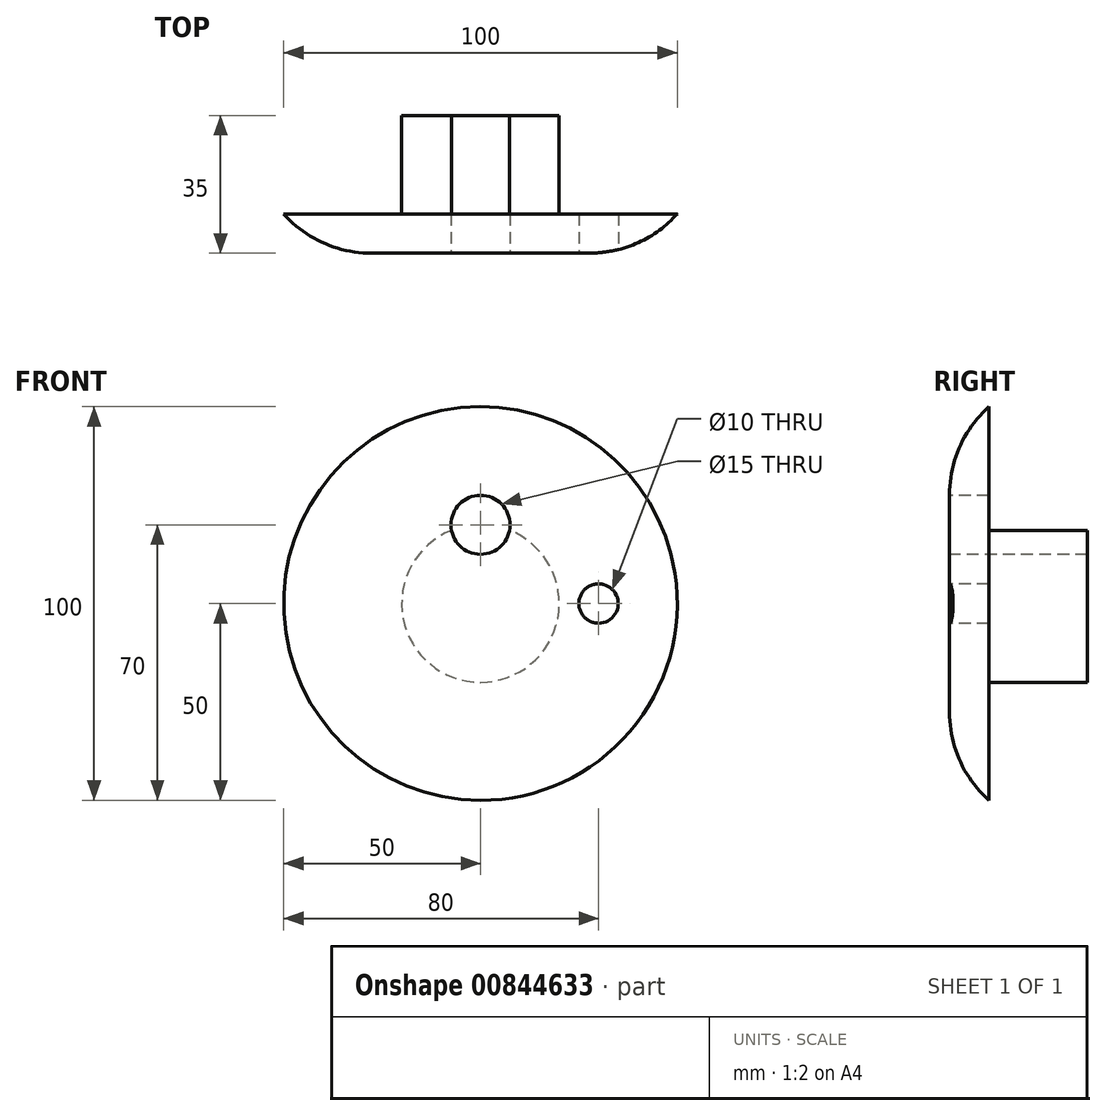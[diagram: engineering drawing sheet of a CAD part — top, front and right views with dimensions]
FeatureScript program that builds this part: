
annotation { "Feature Type Name" : "Feature", "Feature Type Description" : "" }
export const myFeature = defineFeature(function(context is Context, id is Id, definition is map)
    precondition{}
    {
        {
            var Q0;
            Q0=qCreatedBy(makeId("Front.planeOp"),FACE);
            var sketch = newSketch(context, id + "F0", { "sketchPlane" : qUnion([Q0])});
            skCircle(sketch, "E0", {"center": v(0, 0) * mm, "radius": 50 * mm});
            skSolve(sketch);
        }
        {
            var Q0;
            Q0=makeQuery(id+"F0.imprint","IMPRINT",FACE,{"disambiguationData":[TD([[makeQuery(id+"F0.imprint","IMPRINT",EDGE,{"derivedFrom":sQuery(id+"F0.wireOp",EDGE,"E0")}),1.0]])]});
            extrude(context, id + "F1", {"entities" : qUnion([Q0]), "depth" : 10 * mm, "offsetDistance" : 25 * mm});
        }
        {
            var Q0;
            Q0=makeQuery(id+"F1.opExtrude","CAP_FACE",FACE,{"disambiguationData":[OSD([sQuery(id+"F0.wireOp",EDGE,"E0")])],"isStart":true});
            var sketch = newSketch(context, id + "F2", { "sketchPlane" : qUnion([Q0])});
            skCircle(sketch, "E1", {"center": v(0, 0) * mm, "radius": 20 * mm});
            skSolve(sketch);
        }
        {
            var Q0;
            Q0 = qSketchRegion(id + "F2", true);
            extrude(context, id + "F3", {"entities" : qUnion([Q0]), "operationType" : NewBodyOperationType.ADD, "depth" : 25 * mm, "offsetDistance" : 25 * mm});
        }
        {
            var Q0;
            Q0=qCreatedBy(makeId("Front.planeOp"),FACE);
            cPlane(context, id + "F4", {"entities" : qUnion([Q0]), "cplaneType" : CPlaneType.OFFSET, "offset" : 10 * mm, "width" : 150 * mm, "height" : 150 * mm});
        }
        {
            var Q0;
            Q0=qCreatedBy(id+"F4.planeOp",FACE);
            var sketch = newSketch(context, id + "F5", { "sketchPlane" : qUnion([Q0])});
            skCircle(sketch, "E2", {"center": v(30, 0) * mm, "radius": 5 * mm});
            skSolve(sketch);
        }
        {
            var Q0;
            Q0 = qSketchRegion(id + "F5", true);
            extrude(context, id + "F6", {"entities" : qUnion([Q0]), "operationType" : NewBodyOperationType.REMOVE, "oppositeDirection" : true, "depth" : 85.64 * mm, "offsetDistance" : 25 * mm});
        }
        {
            var Q0;
            Q0=makeQuery(id+"F1.opExtrude","CAP_FACE",FACE,{"disambiguationData":[OSD([sQuery(id+"F0.wireOp",EDGE,"E0")])],"isStart":false});
            var sketch = newSketch(context, id + "F7", { "sketchPlane" : qUnion([Q0])});
            skCircle(sketch, "E3", {"center": v(0, 20) * mm, "radius": 7.5 * mm});
            skSolve(sketch);
        }
        {
            var Q0;
            Q0=makeQuery(id+"F7.imprint","IMPRINT",FACE,{"disambiguationData":[TD([[makeQuery(id+"F7.imprint","IMPRINT",EDGE,{"derivedFrom":sQuery(id+"F7.wireOp",EDGE,"E3")}),1.0]])]});
            extrude(context, id + "F8", {"entities" : qUnion([Q0]), "operationType" : NewBodyOperationType.REMOVE, "oppositeDirection" : true, "depth" : 57.22 * mm, "offsetDistance" : 25 * mm});
        }
        {
            var Q0;
            Q0=makeQuery(id+"F1.opExtrude","CAP_EDGE",EDGE,{"disambiguationData":[OSD([sQuery(id+"F0.wireOp",EDGE,"E0")])],"isStart":false});
            fillet(context, id + "F9", {"entities" : qUnion([Q0]), "radius" : 30 * mm, "tangentPropagation" : true, "allowEdgeOverflow" : false});
        }
    });
